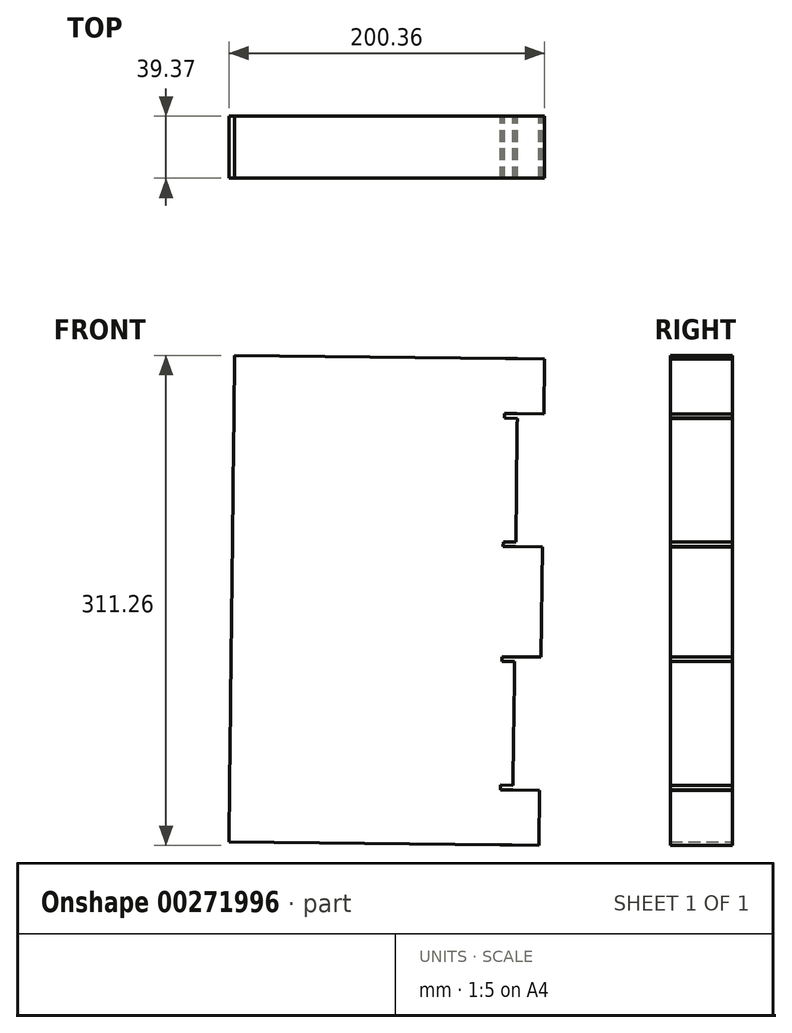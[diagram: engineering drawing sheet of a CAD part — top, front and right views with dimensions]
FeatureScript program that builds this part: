
annotation { "Feature Type Name" : "Feature", "Feature Type Description" : "" }
export const myFeature = defineFeature(function(context is Context, id is Id, definition is map)
    precondition{}
    {
        {
            var Q0;
            Q0=qCreatedBy(makeId("Front.planeOp"),FACE);
            var sketch = newSketch(context, id + "F0", { "sketchPlane" : qUnion([Q0])});
            skLineSegment(sketch, "E0", {"start": v(-127.23, 0) * mm, "end": v(127.23, 0) * mm});
            skLineSegment(sketch, "E1", {"start": v(-254.46, -389.6) * mm, "end": v(-253.36, -293.08) * mm});
            skLineSegment(sketch, "E2", {"start": v(-253.36, -293.08) * mm, "end": v(-253.23, -282) * mm});
            skLineSegment(sketch, "E3", {"start": v(-253.23, -282) * mm, "end": v(-253.1, -270.92) * mm});
            skLineSegment(sketch, "E4", {"start": v(-253.1, -270.92) * mm, "end": v(-252.98, -259.84) * mm});
            skLineSegment(sketch, "E5", {"start": v(-252.98, -259.84) * mm, "end": v(-252.85, -248.76) * mm});
            skLineSegment(sketch, "E6", {"start": v(-252.85, -248.76) * mm, "end": v(-252.73, -237.69) * mm});
            skLineSegment(sketch, "E7", {"start": v(-252.73, -237.69) * mm, "end": v(-252.6, -226.6) * mm});
            skLineSegment(sketch, "E8", {"start": v(-252.6, -226.6) * mm, "end": v(-252.48, -215.53) * mm});
            skLineSegment(sketch, "E9", {"start": v(-252.48, -215.53) * mm, "end": v(-252.35, -204.45) * mm});
            skLineSegment(sketch, "E10", {"start": v(-252.35, -204.45) * mm, "end": v(-252.22, -193.37) * mm});
            skLineSegment(sketch, "E11", {"start": v(-252.22, -193.37) * mm, "end": v(-252.1, -182.3) * mm});
            skLineSegment(sketch, "E12", {"start": v(-252.1, -182.3) * mm, "end": v(-251.97, -171.21) * mm});
            skLineSegment(sketch, "E13", {"start": v(-251.97, -171.21) * mm, "end": v(-251.84, -160.14) * mm});
            skLineSegment(sketch, "E14", {"start": v(-251.84, -160.14) * mm, "end": v(-251.72, -149.06) * mm});
            skLineSegment(sketch, "E15", {"start": v(-251.72, -149.06) * mm, "end": v(-251.6, -137.98) * mm});
            skLineSegment(sketch, "E16", {"start": v(-251.6, -137.98) * mm, "end": v(-251.46, -126.9) * mm});
            skLineSegment(sketch, "E17", {"start": v(-251.46, -126.9) * mm, "end": v(-251.34, -115.82) * mm});
            skLineSegment(sketch, "E18", {"start": v(-251.34, -115.82) * mm, "end": v(-251.21, -104.74) * mm});
            skLineSegment(sketch, "E19", {"start": v(-251.21, -104.74) * mm, "end": v(-251.09, -93.66) * mm});
            skLineSegment(sketch, "E20", {"start": v(-251.09, -93.66) * mm, "end": v(-248.88, 99.36) * mm});
            skLineSegment(sketch, "E21", {"start": v(-248.88, 99.36) * mm, "end": v(-248.76, 110.44) * mm});
            skLineSegment(sketch, "E22", {"start": v(-248.76, 110.44) * mm, "end": v(-248.63, 121.52) * mm});
            skLineSegment(sketch, "E23", {"start": v(-248.63, 121.52) * mm, "end": v(-248.5, 132.6) * mm});
            skLineSegment(sketch, "E24", {"start": v(-248.5, 132.6) * mm, "end": v(-248.38, 143.68) * mm});
            skLineSegment(sketch, "E25", {"start": v(-248.38, 143.68) * mm, "end": v(-248.25, 154.76) * mm});
            skLineSegment(sketch, "E26", {"start": v(-248.25, 154.76) * mm, "end": v(-248.13, 165.84) * mm});
            skLineSegment(sketch, "E27", {"start": v(-248.13, 165.84) * mm, "end": v(-248, 176.91) * mm});
            skLineSegment(sketch, "E28", {"start": v(-248, 176.91) * mm, "end": v(-247.87, 188) * mm});
            skLineSegment(sketch, "E29", {"start": v(-247.87, 188) * mm, "end": v(-247.75, 199.07) * mm});
            skLineSegment(sketch, "E30", {"start": v(-247.75, 199.07) * mm, "end": v(-247.62, 210.15) * mm});
            skLineSegment(sketch, "E31", {"start": v(-247.62, 210.15) * mm, "end": v(-247.5, 221.23) * mm});
            skLineSegment(sketch, "E32", {"start": v(-247.5, 221.23) * mm, "end": v(-247.37, 232.3) * mm});
            skLineSegment(sketch, "E33", {"start": v(-247.37, 232.3) * mm, "end": v(-247.24, 243.39) * mm});
            skLineSegment(sketch, "E34", {"start": v(-247.24, 243.39) * mm, "end": v(-247.12, 254.46) * mm});
            skLineSegment(sketch, "E35", {"start": v(-247.12, 254.46) * mm, "end": v(-246.99, 265.54) * mm});
            skLineSegment(sketch, "E36", {"start": v(-246.99, 265.54) * mm, "end": v(-246.86, 276.62) * mm});
            skLineSegment(sketch, "E37", {"start": v(-246.86, 276.62) * mm, "end": v(-246.74, 287.7) * mm});
            skLineSegment(sketch, "E38", {"start": v(-246.74, 287.7) * mm, "end": v(-246.61, 298.78) * mm});
            skLineSegment(sketch, "E39", {"start": v(-246.61, 298.78) * mm, "end": v(-245.51, 395.3) * mm});
            skLineSegment(sketch, "E40", {"start": v(-245.51, 395.3) * mm, "end": v(191.34, 390.31) * mm});
            skLineSegment(sketch, "E41", {"start": v(191.34, 390.31) * mm, "end": v(192.45, 390.3) * mm});
            skLineSegment(sketch, "E42", {"start": v(192.45, 390.3) * mm, "end": v(193.56, 390.29) * mm});
            skLineSegment(sketch, "E43", {"start": v(193.56, 390.29) * mm, "end": v(194.66, 390.27) * mm});
            skLineSegment(sketch, "E44", {"start": v(194.66, 390.27) * mm, "end": v(195.77, 390.26) * mm});
            skLineSegment(sketch, "E45", {"start": v(195.77, 390.26) * mm, "end": v(196.88, 390.25) * mm});
            skLineSegment(sketch, "E46", {"start": v(196.88, 390.25) * mm, "end": v(197.99, 390.24) * mm});
            skLineSegment(sketch, "E47", {"start": v(197.99, 390.24) * mm, "end": v(199.1, 390.22) * mm});
            skLineSegment(sketch, "E48", {"start": v(199.1, 390.22) * mm, "end": v(200.2, 390.21) * mm});
            skLineSegment(sketch, "E49", {"start": v(200.2, 390.21) * mm, "end": v(201.31, 390.2) * mm});
            skLineSegment(sketch, "E50", {"start": v(201.31, 390.2) * mm, "end": v(202.42, 390.19) * mm});
            skLineSegment(sketch, "E51", {"start": v(202.42, 390.19) * mm, "end": v(203.53, 390.17) * mm});
            skLineSegment(sketch, "E52", {"start": v(203.53, 390.17) * mm, "end": v(204.64, 390.16) * mm});
            skLineSegment(sketch, "E53", {"start": v(204.64, 390.16) * mm, "end": v(205.74, 390.15) * mm});
            skLineSegment(sketch, "E54", {"start": v(205.74, 390.15) * mm, "end": v(206.85, 390.13) * mm});
            skLineSegment(sketch, "E55", {"start": v(206.85, 390.13) * mm, "end": v(207.96, 390.12) * mm});
            skLineSegment(sketch, "E56", {"start": v(207.96, 390.12) * mm, "end": v(209.07, 390.1) * mm});
            skLineSegment(sketch, "E57", {"start": v(209.07, 390.1) * mm, "end": v(210.17, 390.1) * mm});
            skLineSegment(sketch, "E58", {"start": v(210.17, 390.1) * mm, "end": v(211.28, 390.08) * mm});
            skLineSegment(sketch, "E59", {"start": v(211.28, 390.08) * mm, "end": v(254.46, 389.6) * mm});
            skLineSegment(sketch, "E60", {"start": v(254.46, 389.6) * mm, "end": v(253.45, 300.7) * mm});
            skLineSegment(sketch, "E61", {"start": v(253.45, 300.7) * mm, "end": v(210.27, 301.2) * mm});
            skLineSegment(sketch, "E62", {"start": v(210.27, 301.2) * mm, "end": v(209.16, 301.2) * mm});
            skLineSegment(sketch, "E63", {"start": v(209.16, 301.2) * mm, "end": v(208.05, 301.22) * mm});
            skLineSegment(sketch, "E64", {"start": v(208.05, 301.22) * mm, "end": v(206.95, 301.23) * mm});
            skLineSegment(sketch, "E65", {"start": v(206.95, 301.23) * mm, "end": v(205.84, 301.24) * mm});
            skLineSegment(sketch, "E66", {"start": v(205.84, 301.24) * mm, "end": v(204.73, 301.25) * mm});
            skLineSegment(sketch, "E67", {"start": v(204.73, 301.25) * mm, "end": v(203.62, 301.27) * mm});
            skLineSegment(sketch, "E68", {"start": v(203.62, 301.27) * mm, "end": v(202.51, 301.28) * mm});
            skLineSegment(sketch, "E69", {"start": v(202.51, 301.28) * mm, "end": v(201.4, 301.3) * mm});
            skLineSegment(sketch, "E70", {"start": v(201.4, 301.3) * mm, "end": v(200.3, 301.3) * mm});
            skLineSegment(sketch, "E71", {"start": v(200.3, 301.3) * mm, "end": v(199.2, 301.32) * mm});
            skLineSegment(sketch, "E72", {"start": v(199.2, 301.32) * mm, "end": v(198.08, 301.33) * mm});
            skLineSegment(sketch, "E73", {"start": v(198.08, 301.33) * mm, "end": v(196.97, 301.34) * mm});
            skLineSegment(sketch, "E74", {"start": v(196.97, 301.34) * mm, "end": v(195.87, 301.35) * mm});
            skLineSegment(sketch, "E75", {"start": v(195.87, 301.35) * mm, "end": v(194.76, 301.37) * mm});
            skLineSegment(sketch, "E76", {"start": v(194.76, 301.37) * mm, "end": v(193.65, 301.38) * mm});
            skLineSegment(sketch, "E77", {"start": v(193.65, 301.38) * mm, "end": v(192.54, 301.4) * mm});
            skLineSegment(sketch, "E78", {"start": v(192.54, 301.4) * mm, "end": v(191.44, 301.4) * mm});
            skLineSegment(sketch, "E79", {"start": v(191.44, 301.4) * mm, "end": v(190.33, 301.42) * mm});
            skLineSegment(sketch, "E80", {"start": v(190.33, 301.42) * mm, "end": v(190.24, 293.8) * mm});
            skLineSegment(sketch, "E81", {"start": v(190.24, 293.8) * mm, "end": v(210.56, 293.57) * mm});
            skLineSegment(sketch, "E82", {"start": v(210.56, 293.57) * mm, "end": v(210.43, 282.49) * mm});
            skLineSegment(sketch, "E83", {"start": v(210.43, 282.49) * mm, "end": v(210.3, 271.4) * mm});
            skLineSegment(sketch, "E84", {"start": v(210.3, 271.4) * mm, "end": v(210.18, 260.33) * mm});
            skLineSegment(sketch, "E85", {"start": v(210.18, 260.33) * mm, "end": v(210.05, 249.25) * mm});
            skLineSegment(sketch, "E86", {"start": v(210.05, 249.25) * mm, "end": v(209.93, 238.17) * mm});
            skLineSegment(sketch, "E87", {"start": v(209.93, 238.17) * mm, "end": v(209.8, 227.1) * mm});
            skLineSegment(sketch, "E88", {"start": v(209.8, 227.1) * mm, "end": v(209.68, 216.02) * mm});
            skLineSegment(sketch, "E89", {"start": v(209.68, 216.02) * mm, "end": v(209.55, 204.94) * mm});
            skLineSegment(sketch, "E90", {"start": v(209.55, 204.94) * mm, "end": v(209.42, 193.86) * mm});
            skLineSegment(sketch, "E91", {"start": v(209.42, 193.86) * mm, "end": v(209.3, 182.78) * mm});
            skLineSegment(sketch, "E92", {"start": v(209.3, 182.78) * mm, "end": v(209.17, 171.7) * mm});
            skLineSegment(sketch, "E93", {"start": v(209.17, 171.7) * mm, "end": v(209.04, 160.62) * mm});
            skLineSegment(sketch, "E94", {"start": v(209.04, 160.62) * mm, "end": v(208.92, 149.54) * mm});
            skLineSegment(sketch, "E95", {"start": v(208.92, 149.54) * mm, "end": v(208.8, 138.47) * mm});
            skLineSegment(sketch, "E96", {"start": v(208.8, 138.47) * mm, "end": v(208.66, 127.39) * mm});
            skLineSegment(sketch, "E97", {"start": v(208.66, 127.39) * mm, "end": v(208.54, 116.3) * mm});
            skLineSegment(sketch, "E98", {"start": v(208.54, 116.3) * mm, "end": v(208.41, 105.23) * mm});
            skLineSegment(sketch, "E99", {"start": v(208.41, 105.23) * mm, "end": v(208.29, 94.15) * mm});
            skLineSegment(sketch, "E100", {"start": v(208.29, 94.15) * mm, "end": v(187.97, 94.38) * mm});
            skLineSegment(sketch, "E101", {"start": v(187.97, 94.38) * mm, "end": v(187.88, 86.76) * mm});
            skLineSegment(sketch, "E102", {"start": v(187.88, 86.76) * mm, "end": v(188.99, 86.75) * mm});
            skLineSegment(sketch, "E103", {"start": v(188.99, 86.75) * mm, "end": v(190.1, 86.74) * mm});
            skLineSegment(sketch, "E104", {"start": v(190.1, 86.74) * mm, "end": v(191.2, 86.73) * mm});
            skLineSegment(sketch, "E105", {"start": v(191.2, 86.73) * mm, "end": v(192.31, 86.71) * mm});
            skLineSegment(sketch, "E106", {"start": v(192.31, 86.71) * mm, "end": v(193.42, 86.7) * mm});
            skLineSegment(sketch, "E107", {"start": v(193.42, 86.7) * mm, "end": v(194.53, 86.69) * mm});
            skLineSegment(sketch, "E108", {"start": v(194.53, 86.69) * mm, "end": v(195.64, 86.68) * mm});
            skLineSegment(sketch, "E109", {"start": v(195.64, 86.68) * mm, "end": v(196.74, 86.66) * mm});
            skLineSegment(sketch, "E110", {"start": v(196.74, 86.66) * mm, "end": v(197.85, 86.65) * mm});
            skLineSegment(sketch, "E111", {"start": v(197.85, 86.65) * mm, "end": v(198.96, 86.64) * mm});
            skLineSegment(sketch, "E112", {"start": v(198.96, 86.64) * mm, "end": v(200.07, 86.62) * mm});
            skLineSegment(sketch, "E113", {"start": v(200.07, 86.62) * mm, "end": v(201.17, 86.61) * mm});
            skLineSegment(sketch, "E114", {"start": v(201.17, 86.61) * mm, "end": v(202.28, 86.6) * mm});
            skLineSegment(sketch, "E115", {"start": v(202.28, 86.6) * mm, "end": v(203.4, 86.59) * mm});
            skLineSegment(sketch, "E116", {"start": v(203.4, 86.59) * mm, "end": v(204.5, 86.57) * mm});
            skLineSegment(sketch, "E117", {"start": v(204.5, 86.57) * mm, "end": v(205.6, 86.56) * mm});
            skLineSegment(sketch, "E118", {"start": v(205.6, 86.56) * mm, "end": v(206.71, 86.55) * mm});
            skLineSegment(sketch, "E119", {"start": v(206.71, 86.55) * mm, "end": v(207.82, 86.54) * mm});
            skLineSegment(sketch, "E120", {"start": v(207.82, 86.54) * mm, "end": v(251, 86.04) * mm});
            skLineSegment(sketch, "E121", {"start": v(251, 86.04) * mm, "end": v(248.97, -91.74) * mm});
            skLineSegment(sketch, "E122", {"start": v(248.97, -91.74) * mm, "end": v(205.8, -91.25) * mm});
            skLineSegment(sketch, "E123", {"start": v(205.8, -91.25) * mm, "end": v(204.69, -91.24) * mm});
            skLineSegment(sketch, "E124", {"start": v(204.69, -91.24) * mm, "end": v(203.58, -91.23) * mm});
            skLineSegment(sketch, "E125", {"start": v(203.58, -91.23) * mm, "end": v(202.47, -91.21) * mm});
            skLineSegment(sketch, "E126", {"start": v(202.47, -91.21) * mm, "end": v(201.36, -91.2) * mm});
            skLineSegment(sketch, "E127", {"start": v(201.36, -91.2) * mm, "end": v(200.26, -91.19) * mm});
            skLineSegment(sketch, "E128", {"start": v(200.26, -91.19) * mm, "end": v(199.15, -91.18) * mm});
            skLineSegment(sketch, "E129", {"start": v(199.15, -91.18) * mm, "end": v(198.04, -91.16) * mm});
            skLineSegment(sketch, "E130", {"start": v(198.04, -91.16) * mm, "end": v(196.93, -91.15) * mm});
            skLineSegment(sketch, "E131", {"start": v(196.93, -91.15) * mm, "end": v(195.82, -91.14) * mm});
            skLineSegment(sketch, "E132", {"start": v(195.82, -91.14) * mm, "end": v(194.72, -91.13) * mm});
            skLineSegment(sketch, "E133", {"start": v(194.72, -91.13) * mm, "end": v(193.6, -91.11) * mm});
            skLineSegment(sketch, "E134", {"start": v(193.6, -91.11) * mm, "end": v(192.5, -91.1) * mm});
            skLineSegment(sketch, "E135", {"start": v(192.5, -91.1) * mm, "end": v(191.4, -91.09) * mm});
            skLineSegment(sketch, "E136", {"start": v(191.4, -91.09) * mm, "end": v(190.28, -91.08) * mm});
            skLineSegment(sketch, "E137", {"start": v(190.28, -91.08) * mm, "end": v(189.18, -91.06) * mm});
            skLineSegment(sketch, "E138", {"start": v(189.18, -91.06) * mm, "end": v(188.07, -91.05) * mm});
            skLineSegment(sketch, "E139", {"start": v(188.07, -91.05) * mm, "end": v(186.96, -91.04) * mm});
            skLineSegment(sketch, "E140", {"start": v(186.96, -91.04) * mm, "end": v(185.85, -91.02) * mm});
            skLineSegment(sketch, "E141", {"start": v(185.85, -91.02) * mm, "end": v(185.77, -98.64) * mm});
            skLineSegment(sketch, "E142", {"start": v(185.77, -98.64) * mm, "end": v(206.08, -98.88) * mm});
            skLineSegment(sketch, "E143", {"start": v(206.08, -98.88) * mm, "end": v(205.96, -109.95) * mm});
            skLineSegment(sketch, "E144", {"start": v(205.96, -109.95) * mm, "end": v(205.83, -121.03) * mm});
            skLineSegment(sketch, "E145", {"start": v(205.83, -121.03) * mm, "end": v(205.7, -132.11) * mm});
            skLineSegment(sketch, "E146", {"start": v(205.7, -132.11) * mm, "end": v(205.58, -143.2) * mm});
            skLineSegment(sketch, "E147", {"start": v(205.58, -143.2) * mm, "end": v(205.45, -154.27) * mm});
            skLineSegment(sketch, "E148", {"start": v(205.45, -154.27) * mm, "end": v(205.33, -165.35) * mm});
            skLineSegment(sketch, "E149", {"start": v(205.33, -165.35) * mm, "end": v(205.2, -176.43) * mm});
            skLineSegment(sketch, "E150", {"start": v(205.2, -176.43) * mm, "end": v(205.07, -187.5) * mm});
            skLineSegment(sketch, "E151", {"start": v(205.07, -187.5) * mm, "end": v(204.95, -198.58) * mm});
            skLineSegment(sketch, "E152", {"start": v(204.95, -198.58) * mm, "end": v(204.82, -209.66) * mm});
            skLineSegment(sketch, "E153", {"start": v(204.82, -209.66) * mm, "end": v(204.7, -220.74) * mm});
            skLineSegment(sketch, "E154", {"start": v(204.7, -220.74) * mm, "end": v(204.57, -231.82) * mm});
            skLineSegment(sketch, "E155", {"start": v(204.57, -231.82) * mm, "end": v(204.44, -242.9) * mm});
            skLineSegment(sketch, "E156", {"start": v(204.44, -242.9) * mm, "end": v(204.32, -253.98) * mm});
            skLineSegment(sketch, "E157", {"start": v(204.32, -253.98) * mm, "end": v(204.19, -265.06) * mm});
            skLineSegment(sketch, "E158", {"start": v(204.19, -265.06) * mm, "end": v(204.06, -276.13) * mm});
            skLineSegment(sketch, "E159", {"start": v(204.06, -276.13) * mm, "end": v(203.94, -287.21) * mm});
            skLineSegment(sketch, "E160", {"start": v(203.94, -287.21) * mm, "end": v(203.81, -298.3) * mm});
            skLineSegment(sketch, "E161", {"start": v(203.81, -298.3) * mm, "end": v(183.5, -298.06) * mm});
            skLineSegment(sketch, "E162", {"start": v(183.5, -298.06) * mm, "end": v(183.4, -305.68) * mm});
            skLineSegment(sketch, "E163", {"start": v(183.4, -305.68) * mm, "end": v(184.51, -305.7) * mm});
            skLineSegment(sketch, "E164", {"start": v(184.51, -305.7) * mm, "end": v(185.62, -305.7) * mm});
            skLineSegment(sketch, "E165", {"start": v(185.62, -305.7) * mm, "end": v(186.73, -305.72) * mm});
            skLineSegment(sketch, "E166", {"start": v(186.73, -305.72) * mm, "end": v(187.84, -305.73) * mm});
            skLineSegment(sketch, "E167", {"start": v(187.84, -305.73) * mm, "end": v(188.94, -305.74) * mm});
            skLineSegment(sketch, "E168", {"start": v(188.94, -305.74) * mm, "end": v(190.05, -305.75) * mm});
            skLineSegment(sketch, "E169", {"start": v(190.05, -305.75) * mm, "end": v(191.16, -305.77) * mm});
            skLineSegment(sketch, "E170", {"start": v(191.16, -305.77) * mm, "end": v(192.27, -305.78) * mm});
            skLineSegment(sketch, "E171", {"start": v(192.27, -305.78) * mm, "end": v(193.38, -305.8) * mm});
            skLineSegment(sketch, "E172", {"start": v(193.38, -305.8) * mm, "end": v(194.48, -305.8) * mm});
            skLineSegment(sketch, "E173", {"start": v(194.48, -305.8) * mm, "end": v(195.6, -305.82) * mm});
            skLineSegment(sketch, "E174", {"start": v(195.6, -305.82) * mm, "end": v(196.7, -305.83) * mm});
            skLineSegment(sketch, "E175", {"start": v(196.7, -305.83) * mm, "end": v(197.8, -305.84) * mm});
            skLineSegment(sketch, "E176", {"start": v(197.8, -305.84) * mm, "end": v(198.92, -305.86) * mm});
            skLineSegment(sketch, "E177", {"start": v(198.92, -305.86) * mm, "end": v(200.02, -305.87) * mm});
            skLineSegment(sketch, "E178", {"start": v(200.02, -305.87) * mm, "end": v(201.13, -305.88) * mm});
            skLineSegment(sketch, "E179", {"start": v(201.13, -305.88) * mm, "end": v(202.24, -305.9) * mm});
            skLineSegment(sketch, "E180", {"start": v(202.24, -305.9) * mm, "end": v(203.35, -305.9) * mm});
            skLineSegment(sketch, "E181", {"start": v(203.35, -305.9) * mm, "end": v(246.52, -306.4) * mm});
            skLineSegment(sketch, "E182", {"start": v(246.52, -306.4) * mm, "end": v(245.51, -395.3) * mm});
            skLineSegment(sketch, "E183", {"start": v(245.51, -395.3) * mm, "end": v(202.33, -394.8) * mm});
            skLineSegment(sketch, "E184", {"start": v(202.33, -394.8) * mm, "end": v(201.23, -394.79) * mm});
            skLineSegment(sketch, "E185", {"start": v(201.23, -394.79) * mm, "end": v(200.12, -394.78) * mm});
            skLineSegment(sketch, "E186", {"start": v(200.12, -394.78) * mm, "end": v(199, -394.76) * mm});
            skLineSegment(sketch, "E187", {"start": v(199, -394.76) * mm, "end": v(197.9, -394.75) * mm});
            skLineSegment(sketch, "E188", {"start": v(197.9, -394.75) * mm, "end": v(196.8, -394.74) * mm});
            skLineSegment(sketch, "E189", {"start": v(196.8, -394.74) * mm, "end": v(195.69, -394.72) * mm});
            skLineSegment(sketch, "E190", {"start": v(195.69, -394.72) * mm, "end": v(194.58, -394.71) * mm});
            skLineSegment(sketch, "E191", {"start": v(194.58, -394.71) * mm, "end": v(193.47, -394.7) * mm});
            skLineSegment(sketch, "E192", {"start": v(193.47, -394.7) * mm, "end": v(192.36, -394.69) * mm});
            skLineSegment(sketch, "E193", {"start": v(192.36, -394.69) * mm, "end": v(191.25, -394.67) * mm});
            skLineSegment(sketch, "E194", {"start": v(191.25, -394.67) * mm, "end": v(190.15, -394.66) * mm});
            skLineSegment(sketch, "E195", {"start": v(190.15, -394.66) * mm, "end": v(189.04, -394.65) * mm});
            skLineSegment(sketch, "E196", {"start": v(189.04, -394.65) * mm, "end": v(187.93, -394.64) * mm});
            skLineSegment(sketch, "E197", {"start": v(187.93, -394.64) * mm, "end": v(186.82, -394.62) * mm});
            skLineSegment(sketch, "E198", {"start": v(186.82, -394.62) * mm, "end": v(185.72, -394.61) * mm});
            skLineSegment(sketch, "E199", {"start": v(185.72, -394.61) * mm, "end": v(184.6, -394.6) * mm});
            skLineSegment(sketch, "E200", {"start": v(184.6, -394.6) * mm, "end": v(183.5, -394.59) * mm});
            skLineSegment(sketch, "E201", {"start": v(183.5, -394.59) * mm, "end": v(182.4, -394.57) * mm});
            skLineSegment(sketch, "E202", {"start": v(182.4, -394.57) * mm, "end": v(-254.46, -389.6) * mm});
            skSolve(sketch);
        }
        {
            var Q0;
            Q0=makeQuery(id+"F0.imprint","IMPRINT",FACE,{"disambiguationData":[TD([[makeQuery(id+"F0.imprint","IMPRINT",EDGE,{"derivedFrom":sQuery(id+"F0.wireOp",EDGE,"E1")}),-1.0]])]});
            extrude(context, id + "F1", {"entities" : qUnion([Q0]), "depth" : 100 * mm});
        }
        {
            var Q0;
            Q0=makeQuery(id+"F1.opExtrude","SWEPT_BODY",BODY,{"disambiguationData":[OSD([sQuery(id+"F0.wireOp",EDGE,"E1"),sQuery(id+"F0.wireOp",EDGE,"E2"),sQuery(id+"F0.wireOp",EDGE,"E3"),sQuery(id+"F0.wireOp",EDGE,"E4"),sQuery(id+"F0.wireOp",EDGE,"E5"),sQuery(id+"F0.wireOp",EDGE,"E6"),sQuery(id+"F0.wireOp",EDGE,"E7"),sQuery(id+"F0.wireOp",EDGE,"E8"),sQuery(id+"F0.wireOp",EDGE,"E9"),sQuery(id+"F0.wireOp",EDGE,"E10"),sQuery(id+"F0.wireOp",EDGE,"E11"),sQuery(id+"F0.wireOp",EDGE,"E12"),sQuery(id+"F0.wireOp",EDGE,"E13"),sQuery(id+"F0.wireOp",EDGE,"E14"),sQuery(id+"F0.wireOp",EDGE,"E15"),sQuery(id+"F0.wireOp",EDGE,"E16"),sQuery(id+"F0.wireOp",EDGE,"E17"),sQuery(id+"F0.wireOp",EDGE,"E18"),sQuery(id+"F0.wireOp",EDGE,"E19"),sQuery(id+"F0.wireOp",EDGE,"E20"),sQuery(id+"F0.wireOp",EDGE,"E21"),sQuery(id+"F0.wireOp",EDGE,"E22"),sQuery(id+"F0.wireOp",EDGE,"E23"),sQuery(id+"F0.wireOp",EDGE,"E24"),sQuery(id+"F0.wireOp",EDGE,"E25"),sQuery(id+"F0.wireOp",EDGE,"E26"),sQuery(id+"F0.wireOp",EDGE,"E27"),sQuery(id+"F0.wireOp",EDGE,"E28"),sQuery(id+"F0.wireOp",EDGE,"E29"),sQuery(id+"F0.wireOp",EDGE,"E30"),sQuery(id+"F0.wireOp",EDGE,"E31"),sQuery(id+"F0.wireOp",EDGE,"E32"),sQuery(id+"F0.wireOp",EDGE,"E33"),sQuery(id+"F0.wireOp",EDGE,"E34"),sQuery(id+"F0.wireOp",EDGE,"E35"),sQuery(id+"F0.wireOp",EDGE,"E36"),sQuery(id+"F0.wireOp",EDGE,"E37"),sQuery(id+"F0.wireOp",EDGE,"E38"),sQuery(id+"F0.wireOp",EDGE,"E39"),sQuery(id+"F0.wireOp",EDGE,"E40"),sQuery(id+"F0.wireOp",EDGE,"E41"),sQuery(id+"F0.wireOp",EDGE,"E42"),sQuery(id+"F0.wireOp",EDGE,"E43"),sQuery(id+"F0.wireOp",EDGE,"E44"),sQuery(id+"F0.wireOp",EDGE,"E45"),sQuery(id+"F0.wireOp",EDGE,"E46"),sQuery(id+"F0.wireOp",EDGE,"E47"),sQuery(id+"F0.wireOp",EDGE,"E48"),sQuery(id+"F0.wireOp",EDGE,"E49"),sQuery(id+"F0.wireOp",EDGE,"E50"),sQuery(id+"F0.wireOp",EDGE,"E51"),sQuery(id+"F0.wireOp",EDGE,"E52"),sQuery(id+"F0.wireOp",EDGE,"E53"),sQuery(id+"F0.wireOp",EDGE,"E54"),sQuery(id+"F0.wireOp",EDGE,"E55"),sQuery(id+"F0.wireOp",EDGE,"E56"),sQuery(id+"F0.wireOp",EDGE,"E57"),sQuery(id+"F0.wireOp",EDGE,"E58"),sQuery(id+"F0.wireOp",EDGE,"E59"),sQuery(id+"F0.wireOp",EDGE,"E60"),sQuery(id+"F0.wireOp",EDGE,"E61"),sQuery(id+"F0.wireOp",EDGE,"E62"),sQuery(id+"F0.wireOp",EDGE,"E63"),sQuery(id+"F0.wireOp",EDGE,"E64"),sQuery(id+"F0.wireOp",EDGE,"E65"),sQuery(id+"F0.wireOp",EDGE,"E66"),sQuery(id+"F0.wireOp",EDGE,"E67"),sQuery(id+"F0.wireOp",EDGE,"E68"),sQuery(id+"F0.wireOp",EDGE,"E69"),sQuery(id+"F0.wireOp",EDGE,"E70"),sQuery(id+"F0.wireOp",EDGE,"E71"),sQuery(id+"F0.wireOp",EDGE,"E72"),sQuery(id+"F0.wireOp",EDGE,"E73"),sQuery(id+"F0.wireOp",EDGE,"E74"),sQuery(id+"F0.wireOp",EDGE,"E75"),sQuery(id+"F0.wireOp",EDGE,"E76"),sQuery(id+"F0.wireOp",EDGE,"E77"),sQuery(id+"F0.wireOp",EDGE,"E78"),sQuery(id+"F0.wireOp",EDGE,"E79"),sQuery(id+"F0.wireOp",EDGE,"E80"),sQuery(id+"F0.wireOp",EDGE,"E81"),sQuery(id+"F0.wireOp",EDGE,"E82"),sQuery(id+"F0.wireOp",EDGE,"E83"),sQuery(id+"F0.wireOp",EDGE,"E84"),sQuery(id+"F0.wireOp",EDGE,"E85"),sQuery(id+"F0.wireOp",EDGE,"E86"),sQuery(id+"F0.wireOp",EDGE,"E87"),sQuery(id+"F0.wireOp",EDGE,"E88"),sQuery(id+"F0.wireOp",EDGE,"E89"),sQuery(id+"F0.wireOp",EDGE,"E90"),sQuery(id+"F0.wireOp",EDGE,"E91"),sQuery(id+"F0.wireOp",EDGE,"E92"),sQuery(id+"F0.wireOp",EDGE,"E93"),sQuery(id+"F0.wireOp",EDGE,"E94"),sQuery(id+"F0.wireOp",EDGE,"E95"),sQuery(id+"F0.wireOp",EDGE,"E96"),sQuery(id+"F0.wireOp",EDGE,"E97"),sQuery(id+"F0.wireOp",EDGE,"E98"),sQuery(id+"F0.wireOp",EDGE,"E99"),sQuery(id+"F0.wireOp",EDGE,"E100"),sQuery(id+"F0.wireOp",EDGE,"E101"),sQuery(id+"F0.wireOp",EDGE,"E102"),sQuery(id+"F0.wireOp",EDGE,"E103"),sQuery(id+"F0.wireOp",EDGE,"E104"),sQuery(id+"F0.wireOp",EDGE,"E105"),sQuery(id+"F0.wireOp",EDGE,"E106"),sQuery(id+"F0.wireOp",EDGE,"E107"),sQuery(id+"F0.wireOp",EDGE,"E108"),sQuery(id+"F0.wireOp",EDGE,"E109"),sQuery(id+"F0.wireOp",EDGE,"E110"),sQuery(id+"F0.wireOp",EDGE,"E111"),sQuery(id+"F0.wireOp",EDGE,"E112"),sQuery(id+"F0.wireOp",EDGE,"E113"),sQuery(id+"F0.wireOp",EDGE,"E114"),sQuery(id+"F0.wireOp",EDGE,"E115"),sQuery(id+"F0.wireOp",EDGE,"E116"),sQuery(id+"F0.wireOp",EDGE,"E117"),sQuery(id+"F0.wireOp",EDGE,"E118"),sQuery(id+"F0.wireOp",EDGE,"E119"),sQuery(id+"F0.wireOp",EDGE,"E120"),sQuery(id+"F0.wireOp",EDGE,"E121"),sQuery(id+"F0.wireOp",EDGE,"E122"),sQuery(id+"F0.wireOp",EDGE,"E123"),sQuery(id+"F0.wireOp",EDGE,"E124"),sQuery(id+"F0.wireOp",EDGE,"E125"),sQuery(id+"F0.wireOp",EDGE,"E126"),sQuery(id+"F0.wireOp",EDGE,"E127"),sQuery(id+"F0.wireOp",EDGE,"E128"),sQuery(id+"F0.wireOp",EDGE,"E129"),sQuery(id+"F0.wireOp",EDGE,"E130"),sQuery(id+"F0.wireOp",EDGE,"E131"),sQuery(id+"F0.wireOp",EDGE,"E132"),sQuery(id+"F0.wireOp",EDGE,"E133"),sQuery(id+"F0.wireOp",EDGE,"E134"),sQuery(id+"F0.wireOp",EDGE,"E135"),sQuery(id+"F0.wireOp",EDGE,"E136"),sQuery(id+"F0.wireOp",EDGE,"E137"),sQuery(id+"F0.wireOp",EDGE,"E138"),sQuery(id+"F0.wireOp",EDGE,"E139"),sQuery(id+"F0.wireOp",EDGE,"E140"),sQuery(id+"F0.wireOp",EDGE,"E141"),sQuery(id+"F0.wireOp",EDGE,"E142"),sQuery(id+"F0.wireOp",EDGE,"E143"),sQuery(id+"F0.wireOp",EDGE,"E144"),sQuery(id+"F0.wireOp",EDGE,"E145"),sQuery(id+"F0.wireOp",EDGE,"E146"),sQuery(id+"F0.wireOp",EDGE,"E147"),sQuery(id+"F0.wireOp",EDGE,"E148"),sQuery(id+"F0.wireOp",EDGE,"E149"),sQuery(id+"F0.wireOp",EDGE,"E150"),sQuery(id+"F0.wireOp",EDGE,"E151"),sQuery(id+"F0.wireOp",EDGE,"E152"),sQuery(id+"F0.wireOp",EDGE,"E153"),sQuery(id+"F0.wireOp",EDGE,"E154"),sQuery(id+"F0.wireOp",EDGE,"E155"),sQuery(id+"F0.wireOp",EDGE,"E156"),sQuery(id+"F0.wireOp",EDGE,"E157"),sQuery(id+"F0.wireOp",EDGE,"E158"),sQuery(id+"F0.wireOp",EDGE,"E159"),sQuery(id+"F0.wireOp",EDGE,"E160"),sQuery(id+"F0.wireOp",EDGE,"E161"),sQuery(id+"F0.wireOp",EDGE,"E162"),sQuery(id+"F0.wireOp",EDGE,"E163"),sQuery(id+"F0.wireOp",EDGE,"E164"),sQuery(id+"F0.wireOp",EDGE,"E165"),sQuery(id+"F0.wireOp",EDGE,"E166"),sQuery(id+"F0.wireOp",EDGE,"E167"),sQuery(id+"F0.wireOp",EDGE,"E168"),sQuery(id+"F0.wireOp",EDGE,"E169"),sQuery(id+"F0.wireOp",EDGE,"E170"),sQuery(id+"F0.wireOp",EDGE,"E171"),sQuery(id+"F0.wireOp",EDGE,"E172"),sQuery(id+"F0.wireOp",EDGE,"E173"),sQuery(id+"F0.wireOp",EDGE,"E174"),sQuery(id+"F0.wireOp",EDGE,"E175"),sQuery(id+"F0.wireOp",EDGE,"E176"),sQuery(id+"F0.wireOp",EDGE,"E177"),sQuery(id+"F0.wireOp",EDGE,"E178"),sQuery(id+"F0.wireOp",EDGE,"E179"),sQuery(id+"F0.wireOp",EDGE,"E180"),sQuery(id+"F0.wireOp",EDGE,"E181"),sQuery(id+"F0.wireOp",EDGE,"E182"),sQuery(id+"F0.wireOp",EDGE,"E183"),sQuery(id+"F0.wireOp",EDGE,"E184"),sQuery(id+"F0.wireOp",EDGE,"E185"),sQuery(id+"F0.wireOp",EDGE,"E186"),sQuery(id+"F0.wireOp",EDGE,"E187"),sQuery(id+"F0.wireOp",EDGE,"E188"),sQuery(id+"F0.wireOp",EDGE,"E189"),sQuery(id+"F0.wireOp",EDGE,"E190"),sQuery(id+"F0.wireOp",EDGE,"E191"),sQuery(id+"F0.wireOp",EDGE,"E192"),sQuery(id+"F0.wireOp",EDGE,"E193"),sQuery(id+"F0.wireOp",EDGE,"E194"),sQuery(id+"F0.wireOp",EDGE,"E195"),sQuery(id+"F0.wireOp",EDGE,"E196"),sQuery(id+"F0.wireOp",EDGE,"E197"),sQuery(id+"F0.wireOp",EDGE,"E198"),sQuery(id+"F0.wireOp",EDGE,"E199"),sQuery(id+"F0.wireOp",EDGE,"E200"),sQuery(id+"F0.wireOp",EDGE,"E201"),sQuery(id+"F0.wireOp",EDGE,"E202")])]});
            var Q1;
            Q1=qCreatedBy(makeId("Origin.pointOp"),VERTEX);
            transform(context, id + "F2", {"entities" : qUnion([Q0]), "transformType" : TransformType.SCALE_UNIFORMLY, "scale" : .3937, "scalePoint" : qUnion([Q1]), "makeCopy" : false});
        }
    });
